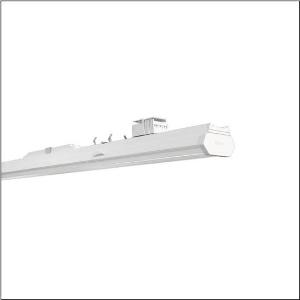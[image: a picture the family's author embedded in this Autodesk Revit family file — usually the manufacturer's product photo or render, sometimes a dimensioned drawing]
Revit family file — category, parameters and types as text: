
# Revit family: licross_r__11_protected_mo_51tp11mn495g_eae0
name_source: partatom
category: Lighting Fixtures
units: mm (PartAtom-declared; Revit-internal decimal feet)

## family parameters
Cut with Voids When Loaded = No
Host = Face
Light Source = No
Part Type = Normal
Room Calculation Point = No
Round Connector Dimension = Use Diameter
Shared = No

## types (1)
- --- (1 x LED, 9980 lm, 55.3 W, 4000K)
    Apparent Load = 55 VA
    CIE Flux Codes = 83 94 98 100 100
    Color Rendering = 80
    Color Temperature = 4000K
    Default Elevation = 1800 mm
    Description = Licross® 11 Protected MO, luminaire insert, of sheet steel, galvanised, coil coated, white, length: 1.500mm, width: 90mm, height: 101mm, LED rated luminous flux: 9.980lm, light colour: 840, control gear: ON/OFF Multilumen, with plug, 3-pole, with phase selection, mains connection: 220..240V, AC, 50/60Hz, rated input power: 55W, halogen-free wiring, primary light control with lens, of plastic, primary optical cover: cover, of PMMA, light emission: direct distribution, primary light characteristic: symmetric, protection rating (complete): IP64, insulation class (complete): insulation class I (protective earthing), certification: CE, ENEC, VDE, UKCA, protection symbol: D if used in an environment with conductive dust loads with corresponding accessories, impact resistance: IK06, permissible ambient temperature for indoor applications: -35..+40°C, corresponds to IFS (International Featured Standards) requirements for safety and quality in the food industry, reducing of maximum allowable ambient temperature of 5°C with ceiling mounting, LABS conformity tested according to VDMA 24364:2018-05, packaging unit: 1 piece
    Height = 92 mm
    Lamp = 1 x LED
    Lamp Light Flux = 9980 lm
    Lamp Power = 55.3 W
    Lamp count = 1
    Length = 1500 mm
    Luminous efficacy = 180 lm/W
    Manufacturer = Siteco
    ModVariant = No
    Model = 51TP11MN495G
    Mounting Place = Ceiling
    Mounting Type = Pendant
    Number of Poles = 1
    OnlyDefault = Yes
    Power Factor = 1
    Product Name = Licross® 11 Protected MO
    Product group = luminaire insert
    ProductGroupID = 901
    Protection Class = Protection class I
    Protection Degree = IP 64
    RLX_Detail_Level = 1
    RLX_Emergency_Light_Flux = 0 lm
    RLX_Emergency_Type = 0
    RLX_Emergency_Type_DB = No
    RlxData = <blob elided: 21805 chars, md5=9480211b>
    Socket = socket
    Standby Power = 0 W
    System Light Flux = 9980 lm
    System Power = 55 W
    Type Comments = factory setting: luminous flux: 100 % | (A | C | E) | 126 mA
    Type Image = l_1256148.jpg
    URL = http://relux.com
    VarID = @adj_019297
    Voltage = 0 V
    Weight = 0.00 kg
    Width = 88 mm

## geometry (parser evidence)
native form markers: Blend x4, Sweep x11
no freeform markers — native parametric forms only
